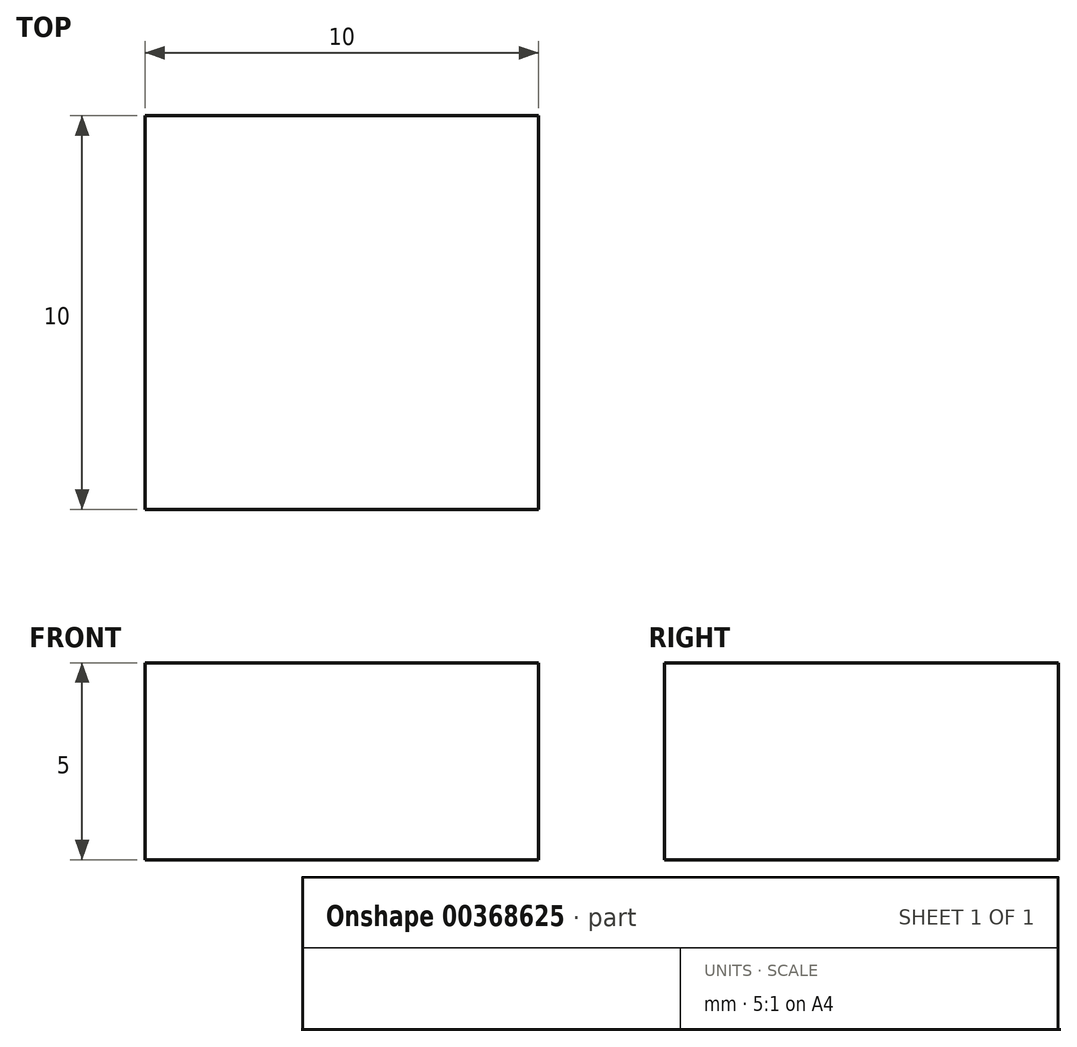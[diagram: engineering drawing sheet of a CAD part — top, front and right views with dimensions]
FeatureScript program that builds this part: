
annotation { "Feature Type Name" : "Feature", "Feature Type Description" : "" }
export const myFeature = defineFeature(function(context is Context, id is Id, definition is map)
    precondition{}
    {
        {
            var Q0;
            Q0=qCreatedBy(makeId("Front.planeOp"),FACE);
            var sketch = newSketch(context, id + "F0", { "sketchPlane" : qUnion([Q0])});
            skLineSegment(sketch, "E0.bottom", {"start": v(0, 0) * mm, "end": v(10, 0) * mm});
            skLineSegment(sketch, "E0.top", {"start": v(0, 5) * mm, "end": v(10, 5) * mm});
            skLineSegment(sketch, "E0.left", {"start": v(0, 0) * mm, "end": v(0, 5) * mm});
            skLineSegment(sketch, "E0.right", {"start": v(10, 0) * mm, "end": v(10, 5) * mm});
            skSolve(sketch);
        }
        {
            var Q0;
            Q0=makeQuery(id+"F0.imprint","IMPRINT",FACE,{"disambiguationData":[TD([[makeQuery(id+"F0.imprint","IMPRINT",EDGE,{"derivedFrom":sQuery(id+"F0.wireOp",EDGE,"E0.bottom")}),1.0]])]});
            extrude(context, id + "F1", {"entities" : qUnion([Q0]), "depth" : 10 * mm});
        }
    });
